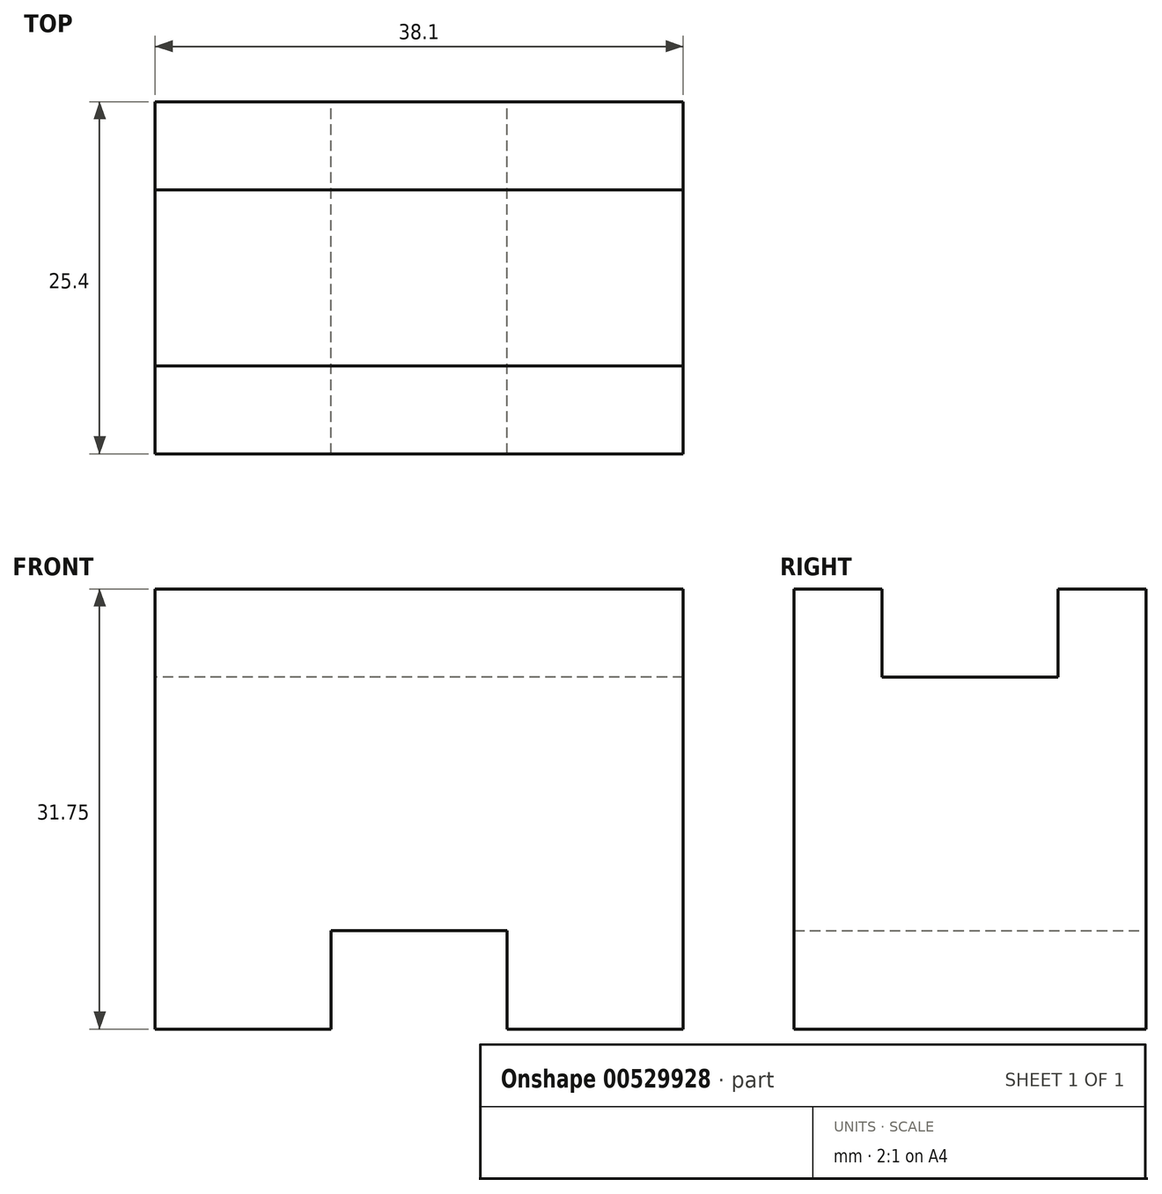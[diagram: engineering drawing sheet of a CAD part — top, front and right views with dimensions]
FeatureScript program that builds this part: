
annotation { "Feature Type Name" : "Feature", "Feature Type Description" : "" }
export const myFeature = defineFeature(function(context is Context, id is Id, definition is map)
    precondition{}
    {
        {
            var Q0;
            Q0=qCreatedBy(makeId("Front.planeOp"),FACE);
            var sketch = newSketch(context, id + "F0", { "sketchPlane" : qUnion([Q0])});
            skLineSegment(sketch, "E0", {"start": v(-38.1, 26.17) * mm, "end": v(0, 26.17) * mm});
            skLineSegment(sketch, "E1", {"start": v(-38.1, 26.17) * mm, "end": v(-38.1, -5.58) * mm});
            skLineSegment(sketch, "E2", {"start": v(0, 26.17) * mm, "end": v(0, -5.58) * mm});
            skLineSegment(sketch, "E3", {"start": v(-38.1, -5.58) * mm, "end": v(-25.4, -5.58) * mm});
            skLineSegment(sketch, "E4", {"start": v(-25.4, -5.58) * mm, "end": v(-25.4, 1.54) * mm});
            skLineSegment(sketch, "E5", {"start": v(-25.4, 1.54) * mm, "end": v(-12.7, 1.54) * mm});
            skLineSegment(sketch, "E6", {"start": v(-12.7, 1.54) * mm, "end": v(-12.7, -5.58) * mm});
            skLineSegment(sketch, "E7", {"start": v(-12.7, -5.58) * mm, "end": v(0, -5.58) * mm});
            skSolve(sketch);
        }
        {
            var Q0;
            Q0=makeQuery(id+"F0.imprint","IMPRINT",FACE,{"disambiguationData":[TD([[makeQuery(id+"F0.imprint","IMPRINT",EDGE,{"derivedFrom":sQuery(id+"F0.wireOp",EDGE,"E0")}),-1.0]])]});
            extrude(context, id + "F1", {"entities" : qUnion([Q0]), "depth" : 25.4 * mm, "offsetDistance" : 25.4 * mm});
        }
        {
            var Q0;
            Q0=makeQuery(id+"F1.opExtrude","SWEPT_FACE",FACE,{"disambiguationData":[OSD([sQuery(id+"F0.wireOp",EDGE,"E1")])]});
            var sketch = newSketch(context, id + "F2", { "sketchPlane" : qUnion([Q0])});
            skLineSegment(sketch, "E8", {"start": v(6.35, 26.17) * mm, "end": v(6.35, 19.82) * mm});
            skLineSegment(sketch, "E9", {"start": v(6.35, 19.82) * mm, "end": v(19.05, 19.82) * mm});
            skLineSegment(sketch, "E10", {"start": v(19.05, 19.82) * mm, "end": v(19.05, 26.17) * mm});
            skSolve(sketch);
        }
        {
            var Q0;
            {var subQ0=sQuery(id+"F2.wireOp",EDGE,"E8");Q0=makeQuery(id+"F2.imprint","IMPRINT",FACE,{"disambiguationData":[TD([[makeQuery(id+"F2.imprint","IMPRINT",EDGE,{"derivedFrom":subQ0}),1.0]])]});}
            extrude(context, id + "F3", {"entities" : qUnion([Q0]), "operationType" : NewBodyOperationType.REMOVE, "endBound" : BoundingType.THROUGH_ALL, "oppositeDirection" : true, "depth" : 25.4 * mm, "offsetDistance" : 25.4 * mm});
        }
    });
